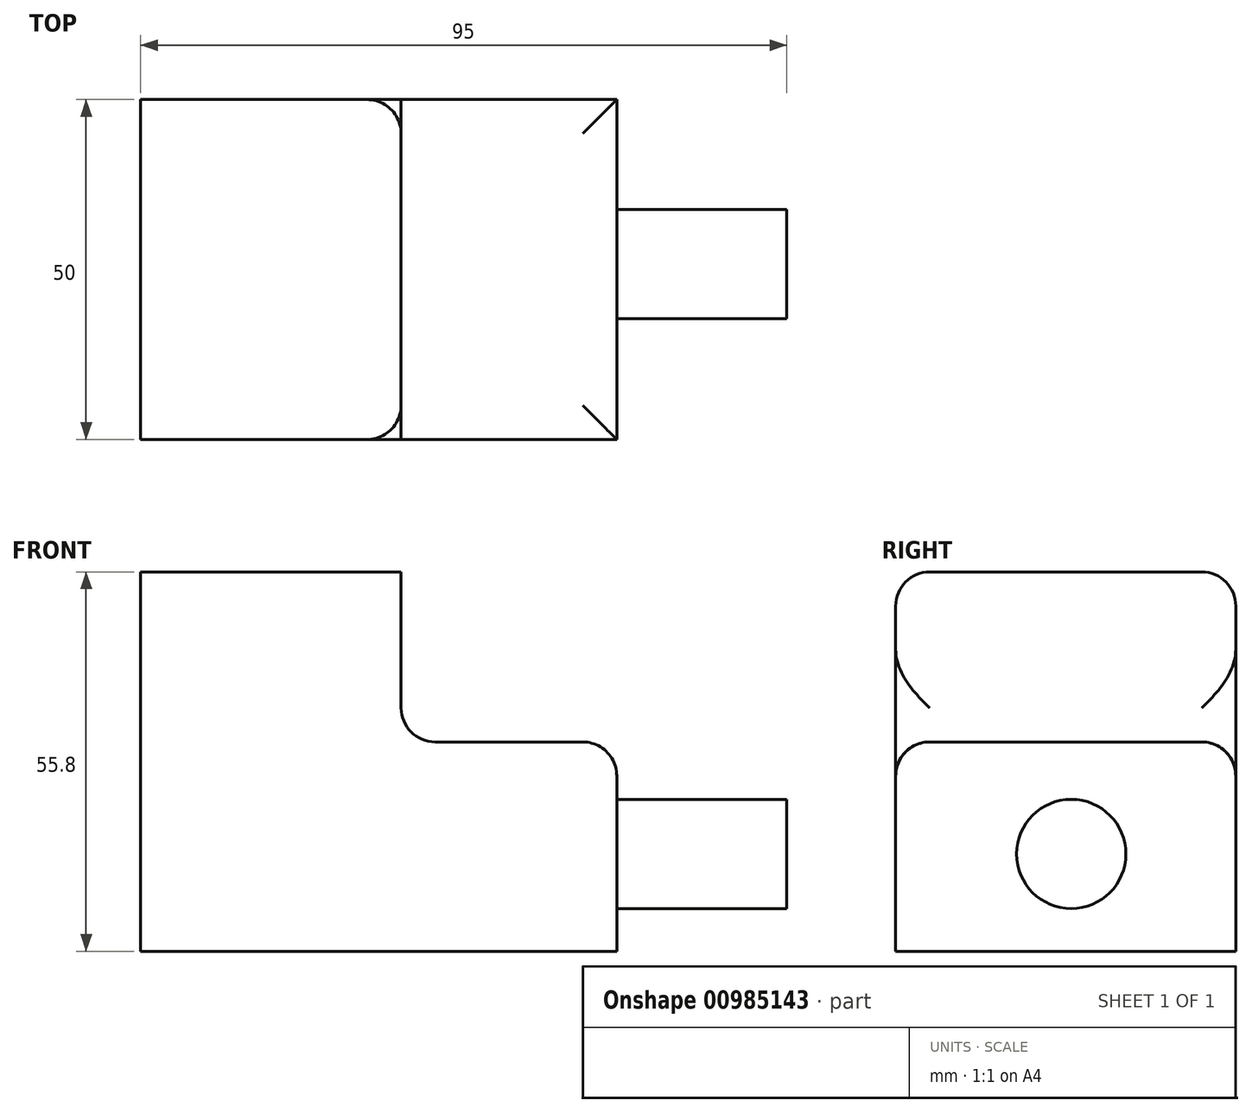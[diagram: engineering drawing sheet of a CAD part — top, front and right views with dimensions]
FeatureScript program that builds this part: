
annotation { "Feature Type Name" : "Feature", "Feature Type Description" : "" }
export const myFeature = defineFeature(function(context is Context, id is Id, definition is map)
    precondition{}
    {
        {
            var Q0;
            Q0=qCreatedBy(makeId("Top.planeOp"),FACE);
            var sketch = newSketch(context, id + "F0", { "sketchPlane" : qUnion([Q0])});
            skLineSegment(sketch, "E0.bottom", {"start": v(-44.04, 24.18) * mm, "end": v(25.96, 24.18) * mm});
            skLineSegment(sketch, "E0.top", {"start": v(-44.04, -25.82) * mm, "end": v(25.96, -25.82) * mm});
            skLineSegment(sketch, "E0.left", {"start": v(-44.04, 24.18) * mm, "end": v(-44.04, -25.82) * mm});
            skLineSegment(sketch, "E0.right", {"start": v(25.96, 24.18) * mm, "end": v(25.96, -25.82) * mm});
            skSolve(sketch);
        }
        {
            var Q0;
            Q0 = qSketchRegion(id + "F0", true);
            extrude(context, id + "F1", {"entities" : qUnion([Q0]), "depth" : 55.8 * mm, "offsetDistance" : 25 * mm});
        }
        {
            var Q0;
            Q0=makeQuery(id+"F1.opExtrude","CAP_EDGE",EDGE,{"disambiguationData":[OSD([sQuery(id+"F0.wireOp",EDGE,"E0.top")])],"isStart":false});
            fillet(context, id + "F2", {"entities" : qUnion([Q0]), "radius" : 5 * mm, "tangentPropagation" : true, "allowEdgeOverflow" : false});
        }
        {
            var Q0;
            Q0=makeQuery(id+"F1.opExtrude","CAP_EDGE",EDGE,{"disambiguationData":[OSD([sQuery(id+"F0.wireOp",EDGE,"E0.bottom")])],"isStart":false});
            fillet(context, id + "F3", {"entities" : qUnion([Q0]), "radius" : 5 * mm, "tangentPropagation" : true, "allowEdgeOverflow" : false});
        }
        {
            var Q0;
            Q0=makeQuery(id+"F1.opExtrude","CAP_FACE",FACE,{"disambiguationData":[OSD([sQuery(id+"F0.wireOp",EDGE,"E0.bottom"),sQuery(id+"F0.wireOp",EDGE,"E0.top"),sQuery(id+"F0.wireOp",EDGE,"E0.left"),sQuery(id+"F0.wireOp",EDGE,"E0.right")])],"isStart":false});
            var sketch = newSketch(context, id + "F4", { "sketchPlane" : qUnion([Q0])});
            skLineSegment(sketch, "E1.bottom", {"start": v(-5.75, 32) * mm, "end": v(30.63, 32) * mm});
            skLineSegment(sketch, "E1.top", {"start": v(-5.75, -34.06) * mm, "end": v(30.63, -34.06) * mm});
            skLineSegment(sketch, "E1.left", {"start": v(-5.75, 32) * mm, "end": v(-5.75, -34.06) * mm});
            skLineSegment(sketch, "E1.right", {"start": v(30.63, 32) * mm, "end": v(30.63, -34.06) * mm});
            skSolve(sketch);
        }
        {
            var Q0;
            {var subQ8=sQuery(id+"F4.wireOp",EDGE,"E1.bottom");Q0=makeQuery(id+"F4.imprint","IMPRINT",FACE,{"disambiguationData":[TD([[makeQuery(id+"F4.imprint","IMPRINT",EDGE,{"derivedFrom":subQ8}),-1.0]])]});}
            var Q1;
            {var subQ1=sQuery(id+"F0.wireOp",EDGE,"E0.right");var subQ9=makeQuery(id+"F1.opExtrude","CAP_EDGE",EDGE,{"disambiguationData":[OSD([subQ1])],"isStart":false});Q1=makeQuery(id+"F4.imprint","IMPRINT",FACE,{"disambiguationData":[TD([[makeQuery(id+"F4.imprint","IMPRINT",EDGE,{"derivedFrom":subQ9}),-1.0]])]});}
            extrude(context, id + "F5", {"entities" : qUnion([Q0, Q1]), "operationType" : NewBodyOperationType.REMOVE, "oppositeDirection" : true, "depth" : 25 * mm, "offsetDistance" : 25 * mm});
        }
        {
            var Q0;
            Q0=makeQuery(id+"F5.boolean.opBoolean","COPY",FACE,{"derivedFrom":makeQuery(id+"F5.opExtrude","CAP_FACE",FACE,{"disambiguationData":[OSD([sQuery(id+"F4.wireOp",EDGE,"E1.bottom"),sQuery(id+"F4.wireOp",EDGE,"E1.top"),sQuery(id+"F4.wireOp",EDGE,"E1.left"),sQuery(id+"F4.wireOp",EDGE,"E1.right")])],"isStart":false})});
            fillet(context, id + "F6", {"entities" : qUnion([Q0]), "radius" : 5 * mm, "tangentPropagation" : true, "allowEdgeOverflow" : false});
        }
        {
            var Q0;
            Q0=makeQuery(id+"F1.opExtrude","SWEPT_FACE",FACE,{"disambiguationData":[OSD([sQuery(id+"F0.wireOp",EDGE,"E0.right")])]});
            var sketch = newSketch(context, id + "F7", { "sketchPlane" : qUnion([Q0])});
            skCircle(sketch, "E2", {"center": v(0, 14.31) * mm, "radius": 8.03 * mm});
            skSolve(sketch);
        }
        {
            var Q0;
            Q0 = qSketchRegion(id + "F7", true);
            extrude(context, id + "F8", {"entities" : qUnion([Q0]), "operationType" : NewBodyOperationType.ADD, "depth" : 25 * mm, "offsetDistance" : 25 * mm});
        }
    });
